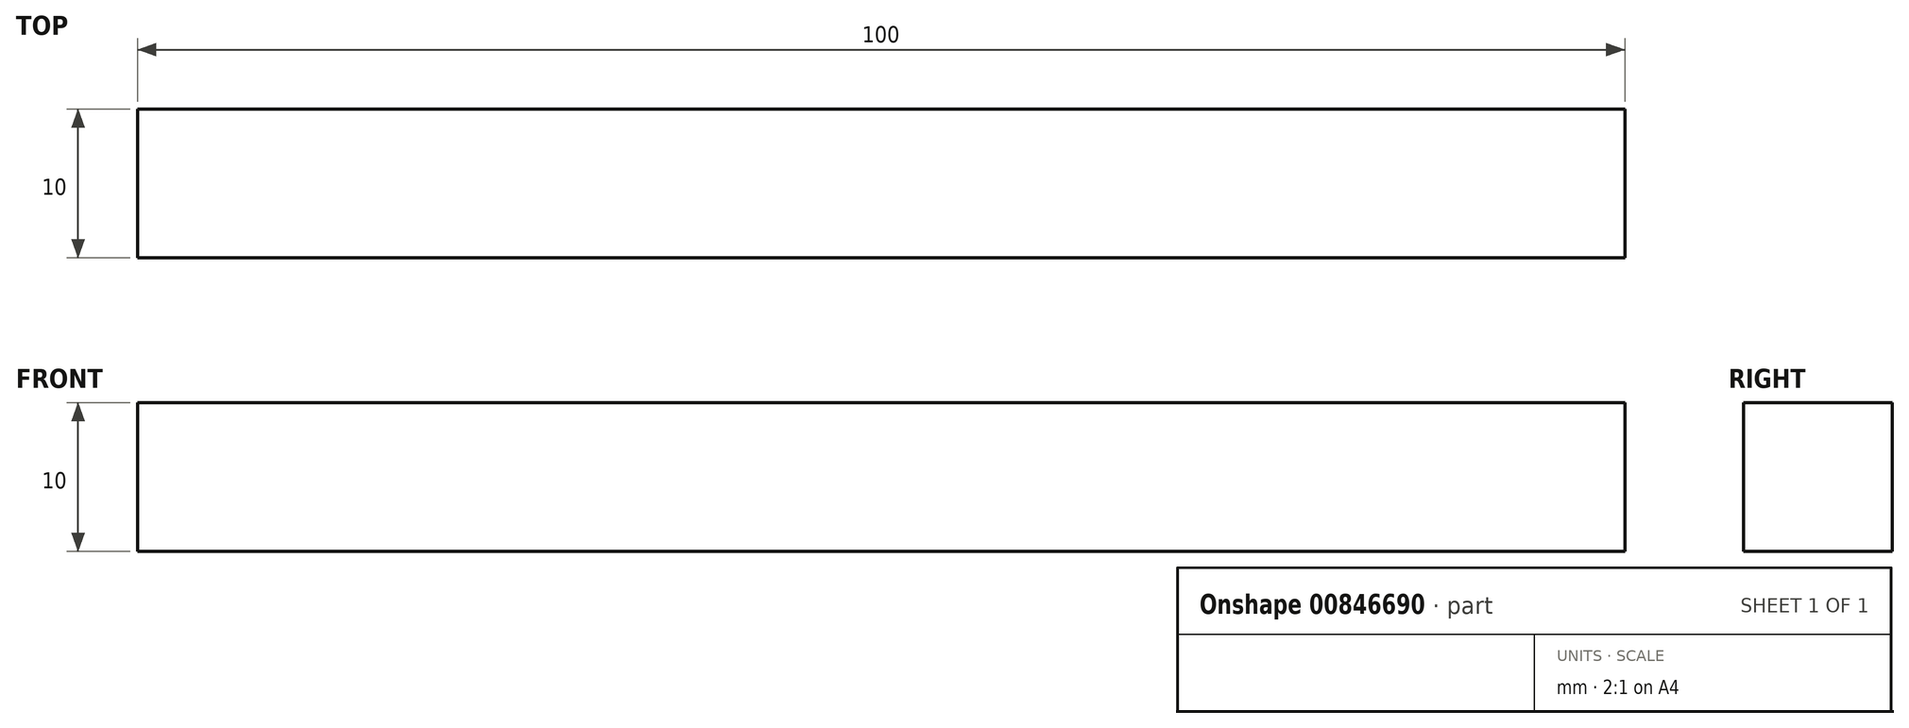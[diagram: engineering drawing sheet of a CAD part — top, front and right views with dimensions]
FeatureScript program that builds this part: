
annotation { "Feature Type Name" : "Feature", "Feature Type Description" : "" }
export const myFeature = defineFeature(function(context is Context, id is Id, definition is map)
    precondition{}
    {
        {
            var Q0;
            Q0=qCreatedBy(makeId("Top.planeOp"),FACE);
            var sketch = newSketch(context, id + "F0", { "sketchPlane" : qUnion([Q0])});
            skLineSegment(sketch, "E0.bottom", {"start": v(-50, -5) * mm, "end": v(50, -5) * mm});
            skLineSegment(sketch, "E0.top", {"start": v(-50, 5) * mm, "end": v(50, 5) * mm});
            skLineSegment(sketch, "E0.left", {"start": v(-50, -5) * mm, "end": v(-50, 5) * mm});
            skLineSegment(sketch, "E0.right", {"start": v(50, -5) * mm, "end": v(50, 5) * mm});
            skPoint(sketch, "E0.middle", {"position": v(0, 0) * mm});
            skSolve(sketch);
        }
        {
            var Q0;
            Q0 = qSketchRegion(id + "F0", true);
            extrude(context, id + "F1", {"entities" : qUnion([Q0]), "depth" : 10 * mm, "offsetDistance" : 25 * mm});
        }
    });
